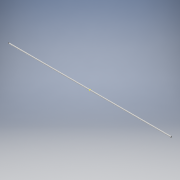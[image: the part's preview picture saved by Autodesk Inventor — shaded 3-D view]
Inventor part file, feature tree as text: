
AUTODESK INVENTOR PART (.ipt)
format: ipt  version: 2017 (Build 210142000, 142)  size: 92,160 bytes
history: native  units: mm
features: extrude x1, sketch x1
ambient origin geometry x8: Origin, YZ Plane, XZ Plane, XY Plane, X Axis, Y Axis, Z Axis, Center Point
bodies: Solid1 (feature_tree)
feature tree (2):
  extrude  "Extrusion1"  Depth=4000.0mm
  sketch  "Sketch1"  dims[d0=26.0mm d1=2.7mm d2=4000.0mm d3=0.0mm]
